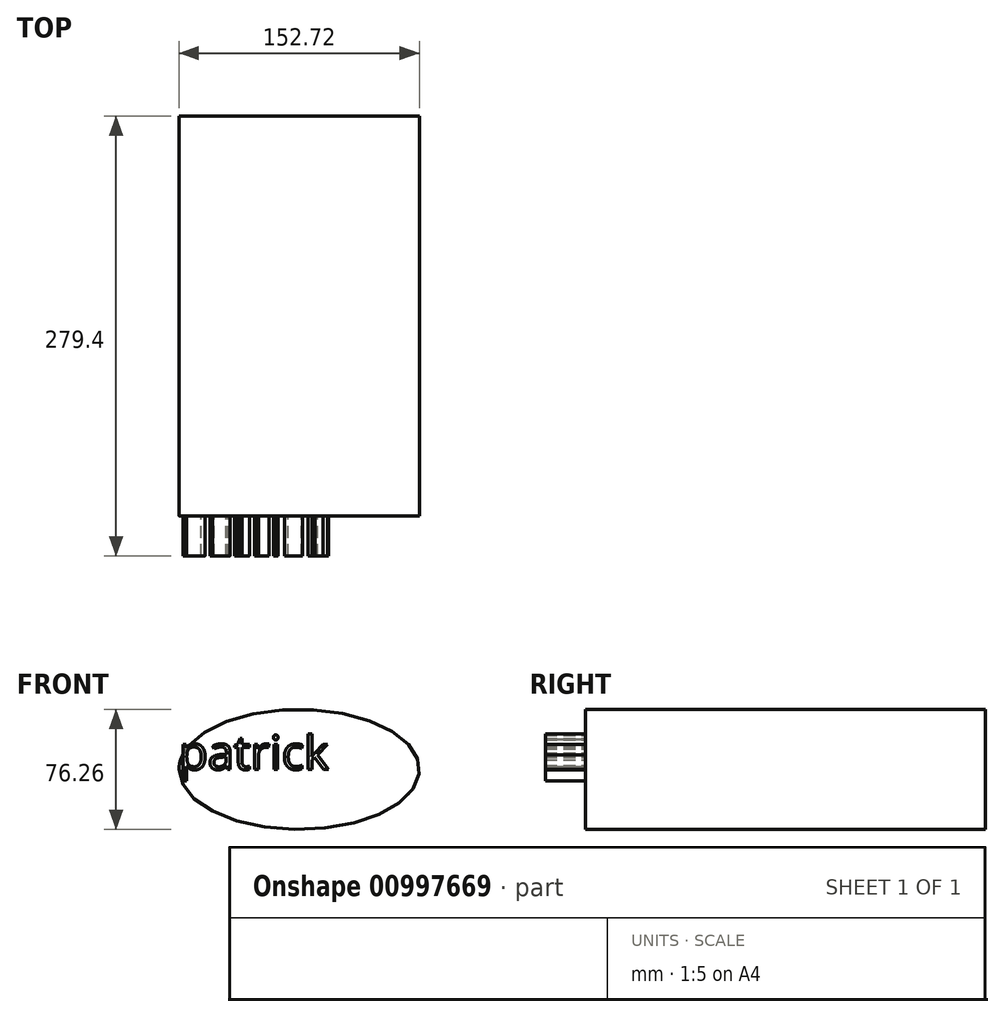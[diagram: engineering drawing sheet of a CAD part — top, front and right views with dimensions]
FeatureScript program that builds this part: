
annotation { "Feature Type Name" : "Feature", "Feature Type Description" : "" }
export const myFeature = defineFeature(function(context is Context, id is Id, definition is map)
    precondition{}
    {
        {
            var Q0;
            Q0=qCreatedBy(makeId("Front.planeOp"),FACE);
            var sketch = newSketch(context, id + "F0", { "sketchPlane" : qUnion([Q0])});
            skEllipse(sketch, "E0", {"center": v(0, 0) * mm, "majorRadius": 76.36 * mm, "minorRadius": 38.13 * mm, "majorAxis": v(-1, 0)});
            skSolve(sketch);
        }
        {
            var Q0;
            Q0=makeQuery(id+"F0.imprint","IMPRINT",FACE,{"disambiguationData":[TD([[makeQuery(id+"F0.imprint","IMPRINT",EDGE,{"derivedFrom":sQuery(id+"F0.wireOp",EDGE,"E0")}),1.0]])]});
            extrude(context, id + "F1", {"entities" : qUnion([Q0]), "depth" : 254 * mm, "offsetDistance" : 25.4 * mm});
        }
        {
            var Q0;
            Q0=makeQuery(id+"F1.opExtrude","CAP_FACE",FACE,{"disambiguationData":[OSD([sQuery(id+"F0.wireOp",EDGE,"E0")])],"isStart":false});
            var sketch = newSketch(context, id + "F2", { "sketchPlane" : qUnion([Q0])});
            skText(sketch, "E1", { "text": "patrick", "fontName": "OpenSans-Regular.ttf"});
            const initialGuessF2  = {"E1": [-0.07636, 0, 1, 0, 0.02152]};
            skSetInitialGuess(sketch, initialGuessF2);
            skSolve(sketch);
        }
        {
            var Q0;
            Q0 = qSketchRegion(id + "F2", true);
            extrude(context, id + "F3", {"entities" : qUnion([Q0]), "operationType" : NewBodyOperationType.ADD, "depth" : 25.4 * mm, "offsetDistance" : 25.4 * mm});
        }
    });
